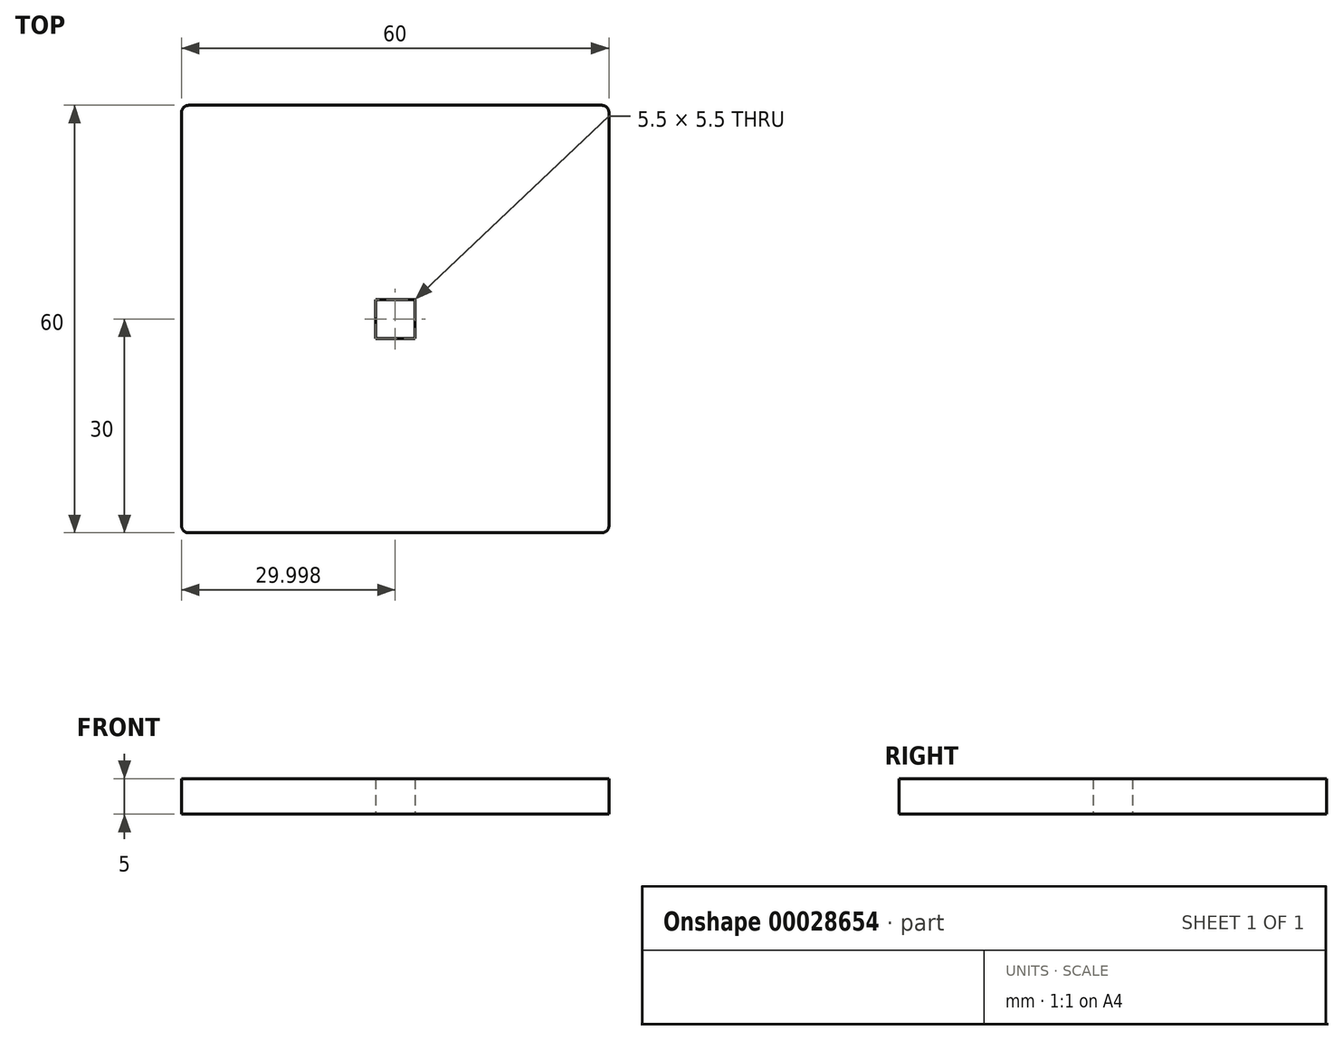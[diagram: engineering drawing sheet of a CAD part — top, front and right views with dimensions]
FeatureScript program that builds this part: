
annotation { "Feature Type Name" : "Feature", "Feature Type Description" : "" }
export const myFeature = defineFeature(function(context is Context, id is Id, definition is map)
    precondition{}
    {
        {
            var Q0;
            Q0=qCreatedBy(makeId("Top.planeOp"),FACE);
            var sketch = newSketch(context, id + "F0", { "sketchPlane" : qUnion([Q0])});
            skLineSegment(sketch, "E0.bottom", {"start": v(-26.57, 30) * mm, "end": v(31.43, 30) * mm});
            skLineSegment(sketch, "E0.top", {"start": v(-26.57, -30) * mm, "end": v(31.43, -30) * mm});
            skLineSegment(sketch, "E0.left", {"start": v(-27.57, 29) * mm, "end": v(-27.57, -29) * mm});
            skLineSegment(sketch, "E0.right", {"start": v(32.43, 29) * mm, "end": v(32.43, -29) * mm});
            skLineSegment(sketch, "E1", {"start": v(-27.57, 0) * mm, "end": v(32.43, 0) * mm, "construction": true});
            skLineSegment(sketch, "E2", {"start": v(2.43, 30) * mm, "end": v(2.43, -30) * mm, "construction": true});
            skLineSegment(sketch, "E3.bottom", {"start": v(-0.32, 2.75) * mm, "end": v(5.18, 2.75) * mm});
            skLineSegment(sketch, "E3.top", {"start": v(-0.32, -2.75) * mm, "end": v(5.18, -2.75) * mm});
            skLineSegment(sketch, "E3.left", {"start": v(-0.32, 2.75) * mm, "end": v(-0.32, -2.75) * mm});
            skLineSegment(sketch, "E3.right", {"start": v(5.18, 2.75) * mm, "end": v(5.18, -2.75) * mm});
            skPoint(sketch, "E4", {"position": v(2.43, 0) * mm});
            skLineSegment(sketch, "E5", {"start": v(-0.32, 0) * mm, "end": v(5.18, 0) * mm, "construction": true});
            skPoint(sketch, "E6.visualSharp", {"position": v(32.43, 30) * mm});
            skArc(sketch, "E6.filletArc", {"start": v(32.43, 29) * mm, "mid": v(32.13, 29.7) * mm, "end": v(31.43, 30) * mm});
            skPoint(sketch, "E7.visualSharp", {"position": v(32.43, -30) * mm});
            skArc(sketch, "E7.filletArc", {"start": v(31.43, -30) * mm, "mid": v(32.13, -29.7) * mm, "end": v(32.43, -29) * mm});
            skPoint(sketch, "E8.visualSharp", {"position": v(-27.57, -30) * mm});
            skArc(sketch, "E8.filletArc", {"start": v(-27.57, -29) * mm, "mid": v(-27.28, -29.7) * mm, "end": v(-26.57, -30) * mm});
            skPoint(sketch, "E9.visualSharp", {"position": v(-27.57, 30) * mm});
            skArc(sketch, "E9.filletArc", {"start": v(-26.57, 30) * mm, "mid": v(-27.28, 29.7) * mm, "end": v(-27.57, 29) * mm});
            skSolve(sketch);
        }
        {
            var Q0;
            Q0 = qSketchRegion(id + "F0", true);
            extrude(context, id + "F1", {"entities" : qUnion([Q0]), "depth" : 5 * mm});
        }
    });
